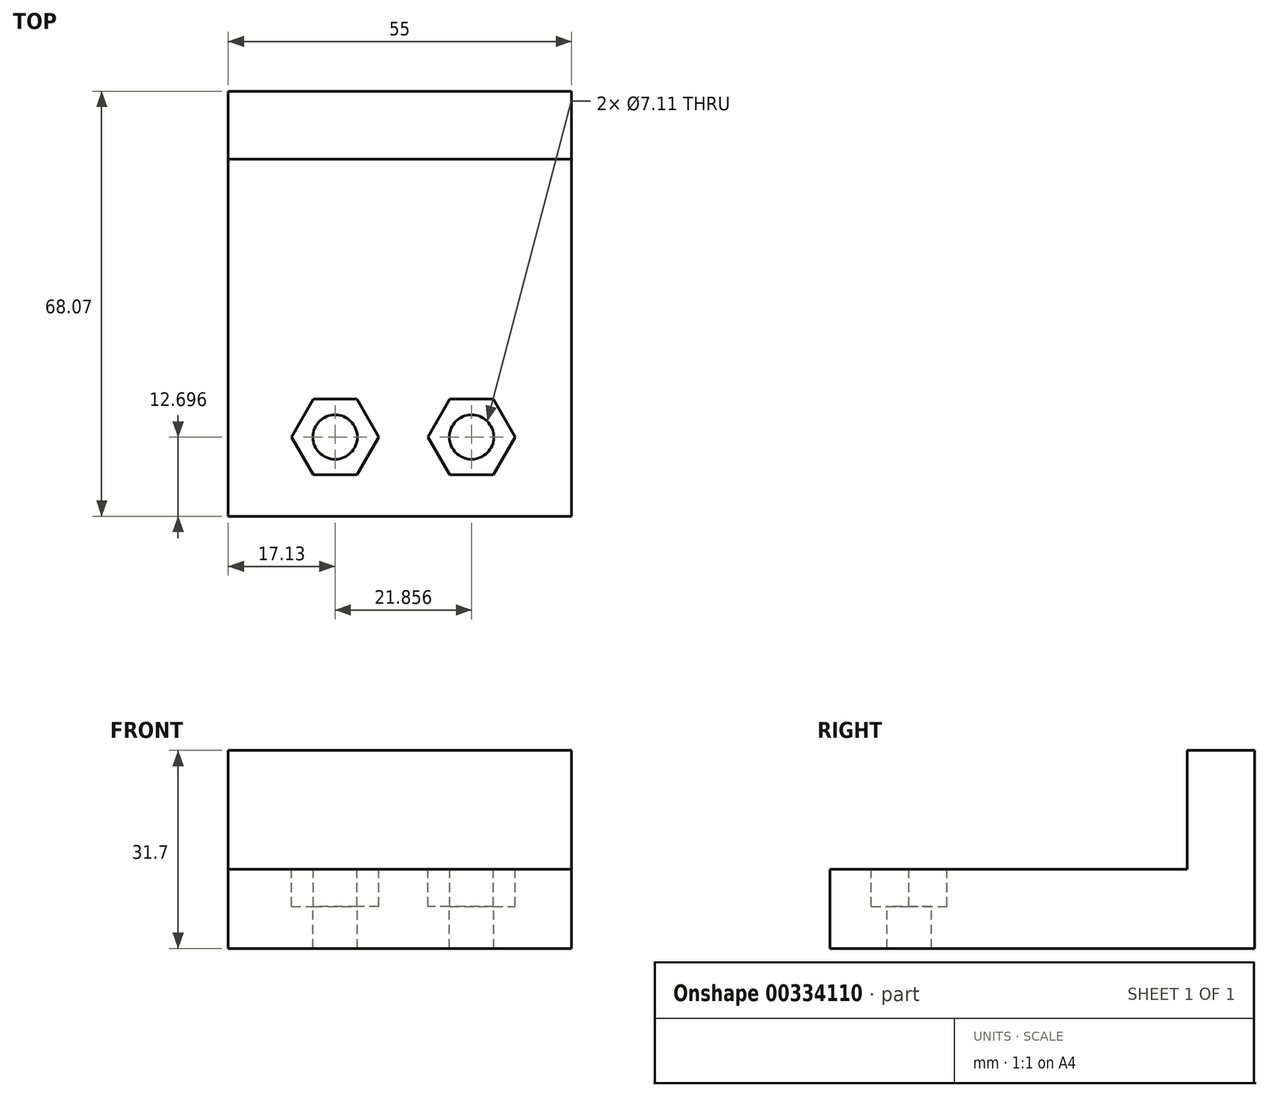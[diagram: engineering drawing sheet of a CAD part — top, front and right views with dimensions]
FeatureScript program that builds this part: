
annotation { "Feature Type Name" : "Feature", "Feature Type Description" : "" }
export const myFeature = defineFeature(function(context is Context, id is Id, definition is map)
    precondition{}
    {
        {
            var Q0;
            Q0=qCreatedBy(makeId("Top.planeOp"),FACE);
            var sketch = newSketch(context, id + "F0", { "sketchPlane" : qUnion([Q0])});
            skLineSegment(sketch, "E0.bottom", {"start": v(-28.03, 27) * mm, "end": v(26.97, 27) * mm});
            skLineSegment(sketch, "E0.top", {"start": v(-28.03, -41.07) * mm, "end": v(26.97, -41.07) * mm});
            skLineSegment(sketch, "E0.left", {"start": v(-28.03, 27) * mm, "end": v(-28.03, -41.07) * mm});
            skLineSegment(sketch, "E0.right", {"start": v(26.97, 27) * mm, "end": v(26.97, -41.07) * mm});
            skSolve(sketch);
        }
        {
            var Q0;
            Q0=makeQuery(id+"F0.imprint","IMPRINT",FACE,{"disambiguationData":[TD([[makeQuery(id+"F0.imprint","IMPRINT",EDGE,{"derivedFrom":sQuery(id+"F0.wireOp",EDGE,"E0.bottom")}),-1.0]])]});
            extrude(context, id + "F1", {"entities" : qUnion([Q0]), "depth" : 12.7 * mm});
        }
        {
            var Q0;
            Q0=makeQuery(id+"F1.opExtrude","CAP_FACE",FACE,{"disambiguationData":[OSD([sQuery(id+"F0.wireOp",EDGE,"E0.bottom"),sQuery(id+"F0.wireOp",EDGE,"E0.top"),sQuery(id+"F0.wireOp",EDGE,"E0.left"),sQuery(id+"F0.wireOp",EDGE,"E0.right")])],"isStart":false});
            var sketch = newSketch(context, id + "F2", { "sketchPlane" : qUnion([Q0])});
            skLineSegment(sketch, "E1", {"start": v(0, -41.07) * mm, "end": v(0, -28.37) * mm});
            skCircle(sketch, "E2", {"center": v(-10.9, -28.37) * mm, "radius": 3.56 * mm});
            skCircle(sketch, "E3", {"center": v(10.96, -28.37) * mm, "radius": 3.56 * mm});
            skLineSegment(sketch, "E4", {"start": v(-17.9, -28.37) * mm, "end": v(-14.4, -22.31) * mm});
            skLineSegment(sketch, "E5", {"start": v(-14.4, -22.31) * mm, "end": v(-7.4, -22.31) * mm});
            skLineSegment(sketch, "E6", {"start": v(-7.4, -22.31) * mm, "end": v(-3.9, -28.37) * mm});
            skLineSegment(sketch, "E7", {"start": v(-14.4, -34.44) * mm, "end": v(-17.9, -28.37) * mm});
            skLineSegment(sketch, "E8", {"start": v(-14.4, -34.44) * mm, "end": v(-7.4, -34.44) * mm});
            skLineSegment(sketch, "E9", {"start": v(-3.9, -28.37) * mm, "end": v(-7.4, -34.44) * mm});
            skLineSegment(sketch, "E10", {"start": v(17.96, -28.37) * mm, "end": v(14.46, -22.31) * mm});
            skLineSegment(sketch, "E11", {"start": v(7.46, -22.31) * mm, "end": v(14.46, -22.31) * mm});
            skLineSegment(sketch, "E12", {"start": v(7.46, -22.31) * mm, "end": v(3.96, -28.37) * mm});
            skLineSegment(sketch, "E13", {"start": v(3.96, -28.37) * mm, "end": v(7.46, -34.44) * mm});
            skLineSegment(sketch, "E14", {"start": v(14.46, -34.44) * mm, "end": v(7.46, -34.44) * mm});
            skLineSegment(sketch, "E15", {"start": v(14.46, -34.44) * mm, "end": v(17.96, -28.37) * mm});
            skSolve(sketch);
        }
        {
            var Q0;
            Q0=makeQuery(id+"F2.imprint","IMPRINT",FACE,{"disambiguationData":[TD([[makeQuery(id+"F2.imprint","IMPRINT",EDGE,{"derivedFrom":sQuery(id+"F2.wireOp",EDGE,"E2")}),-1.0]])]});
            var Q1;
            Q1=makeQuery(id+"F2.imprint","IMPRINT",FACE,{"disambiguationData":[TD([[makeQuery(id+"F2.imprint","IMPRINT",EDGE,{"derivedFrom":sQuery(id+"F2.wireOp",EDGE,"E3")}),-1.0]])]});
            extrude(context, id + "F3", {"entities" : qUnion([Q0, Q1]), "operationType" : NewBodyOperationType.REMOVE, "oppositeDirection" : true, "depth" : 6 * mm});
        }
        {
            var Q0;
            Q0=makeQuery(id+"F3.boolean.opBoolean","SPLIT",FACE,{"disambiguationData":[TD([makeQuery(id+"F3.opExtrude","SWEPT_FACE",FACE,{"disambiguationData":[OSD([sQuery(id+"F2.wireOp",EDGE,"E2")])]})])],"derivedFrom":makeQuery(id+"F1.opExtrude","CAP_FACE",FACE,{"disambiguationData":[OSD([sQuery(id+"F0.wireOp",EDGE,"E0.bottom"),sQuery(id+"F0.wireOp",EDGE,"E0.top"),sQuery(id+"F0.wireOp",EDGE,"E0.left"),sQuery(id+"F0.wireOp",EDGE,"E0.right")])],"isStart":false})});
            var Q1;
            Q1=makeQuery(id+"F3.boolean.opBoolean","SPLIT",FACE,{"disambiguationData":[TD([makeQuery(id+"F3.opExtrude","SWEPT_FACE",FACE,{"disambiguationData":[OSD([sQuery(id+"F2.wireOp",EDGE,"E3")])]})])],"derivedFrom":makeQuery(id+"F1.opExtrude","CAP_FACE",FACE,{"disambiguationData":[OSD([sQuery(id+"F0.wireOp",EDGE,"E0.bottom"),sQuery(id+"F0.wireOp",EDGE,"E0.top"),sQuery(id+"F0.wireOp",EDGE,"E0.left"),sQuery(id+"F0.wireOp",EDGE,"E0.right")])],"isStart":false})});
            extrude(context, id + "F4", {"entities" : qUnion([Q0, Q1]), "operationType" : NewBodyOperationType.REMOVE, "endBound" : BoundingType.UP_TO_NEXT, "oppositeDirection" : true, "depth" : 25.4 * mm});
        }
        {
            var Q0;
            {var subQ0=sQuery(id+"F0.wireOp",EDGE,"E0.bottom");var subQ1=sQuery(id+"F0.wireOp",EDGE,"E0.right");var subQ2=sQuery(id+"F0.wireOp",EDGE,"E0.top");var subQ3=sQuery(id+"F0.wireOp",EDGE,"E0.left");Q0=makeQuery(id+"F3.boolean.opBoolean","SPLIT",FACE,{"disambiguationData":[TD([makeQuery(id+"F1.opExtrude","SWEPT_FACE",FACE,{"disambiguationData":[OSD([subQ0])]})])],"derivedFrom":makeQuery(id+"F1.opExtrude","CAP_FACE",FACE,{"disambiguationData":[OSD([subQ0,subQ2,subQ3,subQ1])],"isStart":false})});}
            var sketch = newSketch(context, id + "F5", { "sketchPlane" : qUnion([Q0])});
            skLineSegment(sketch, "E16.bottom", {"start": v(-28.03, 27) * mm, "end": v(26.97, 27) * mm});
            skLineSegment(sketch, "E16.top", {"start": v(-28.03, 16.14) * mm, "end": v(26.97, 16.14) * mm});
            skLineSegment(sketch, "E16.left", {"start": v(-28.03, 27) * mm, "end": v(-28.03, 16.14) * mm});
            skLineSegment(sketch, "E16.right", {"start": v(26.97, 27) * mm, "end": v(26.97, 16.14) * mm});
            skSolve(sketch);
        }
        {
            var Q0;
            Q0 = qSketchRegion(id + "F5", true);
            extrude(context, id + "F6", {"entities" : qUnion([Q0]), "operationType" : NewBodyOperationType.ADD, "depth" : 19 * mm});
        }
    });
